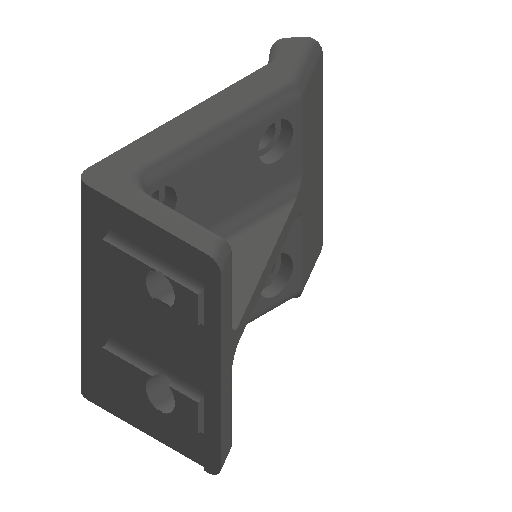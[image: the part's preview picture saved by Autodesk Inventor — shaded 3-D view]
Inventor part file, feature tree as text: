
AUTODESK INVENTOR PART (.ipt)
format: ipt  version: 2024.1 (Build 281209000, 209)  size: 905,728 bytes
history: native  units: in
note: dims shown in document units (in); Inventor stores cm internally (conversion verified against a paired STEP export)
features: extrude x6, projected_geometry x3, sketch x2, hole x2, fillet x2, plane x1
ambient origin geometry x8: Origin, YZ Plane, XZ Plane, XY Plane, X Axis, Y Axis, Z Axis, Center Point
bodies: Solid1 (feature_tree)
feature tree (16):
  sketch  "Sketch1"  dims[d0=0.165in d1=0.165in]
  extrude  "Extrusion1"  Depth=0.165in
  extrude  "Extrusion2"  Depth=0.0625in TaperAngle=0.0deg
  extrude  "Extrusion3"  Depth=0.25in
  hole  "Hole1"  [1 undecoded]
  hole  "Hole2"  [1 undecoded]
  fillet  "Fillet1"  Radius=0.008in
  plane  "Work Plane1"
  extrude  "Extrusion6"  Depth=0.008in
  extrude  "Extrusion7"  Depth=0.008in
  extrude  "Extrusion8"  Depth=1.5in TaperAngle=0.0deg
  fillet  "Fillet8"  Radius=0.5in
  sketch  "Sketch2"  dims[d2=0.3125in d3=0.0in d4=0.0625in d5=0.0in d6=0.25in d8=1.5748in d9=0.7874in d10=0.7874in d11=0.1969in d12=0.2402in d13=0.2402in d14=0.2441in d15=0.0551in d16=0.0276in d17=45.0deg d18=0.0551in d19=360.0deg d20=0.0394in d22=0.0157in d23=0.0157in d24=0.008in d25=0.008in d26=0.008in d27=0.008in d29=1.5in d30=0.0in d31=0.5in d32=0.75in d33=0.25in d34=0.75in d35=0.435in d36=0.125in d37=0.5635in d38=1.0in d39=0.0in d40=0.2in d41=0.75in d42=0.3in d43=0.1in d44=0.5635in d45=1.0in d46=0.0in d47=0.125in d49=0.3in d50=0.3in d51=0.7874in d52=0.375in d53=0.625in d54=0.8071in d58=-0.8125in d67=0.825in d68=0.0in d69=0.0in d70=0.125in d71=0.0in d72=1.625in d73=0.0in d74=0.1in d79=0.2749in d55=0.0in d56=0.0in d57=0.0in]
  projected_geometry  "Projected Loop1"
  projected_geometry  "Projected Loop3"
  projected_geometry  "Projected Loop4"
note: 2 required parameter values undecoded (feature->parameter linkage not recoverable at this tier; creation-order binding heuristic only, values carry confidence <= 0.55)
